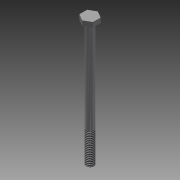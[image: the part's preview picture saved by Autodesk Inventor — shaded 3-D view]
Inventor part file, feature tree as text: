
AUTODESK INVENTOR PART (.ipt)
format: ipt  version: 2015 SP1 (Build 190203100, 203)  size: 111,104 bytes
history: native  units: in
note: dims shown in document units (in); Inventor stores cm internally (conversion verified against a paired STEP export)
features: extrude x2, sketch x2, thread x1
ambient origin geometry x8: Origin, YZ Plane, XZ Plane, XY Plane, X Axis, Y Axis, Z Axis, Center Point
bodies: Solid1 (feature_tree)
feature tree (5):
  extrude  "Extrusion1"  Depth=4.0in TaperAngle=0.0deg
  extrude  "Extrusion2"  Depth=0.4375in
  thread  "Thread1"  [1 undecoded]
  sketch  "Sketch1"  dims[d0=0.25in d1=4.0in d2=0.0in]
  sketch  "Sketch2"  dims[d3=0.4375in d4=0.4375in d5=0.4375in d6=120.0deg d7=120.0deg d8=0.2188in d9=0.2188in d10=0.2188in d11=0.1562in d12=0.0in d13=1.0in d14=3.0in]
note: 1 required parameter value undecoded (feature->parameter linkage not recoverable at this tier; creation-order binding heuristic only, values carry confidence <= 0.55)
